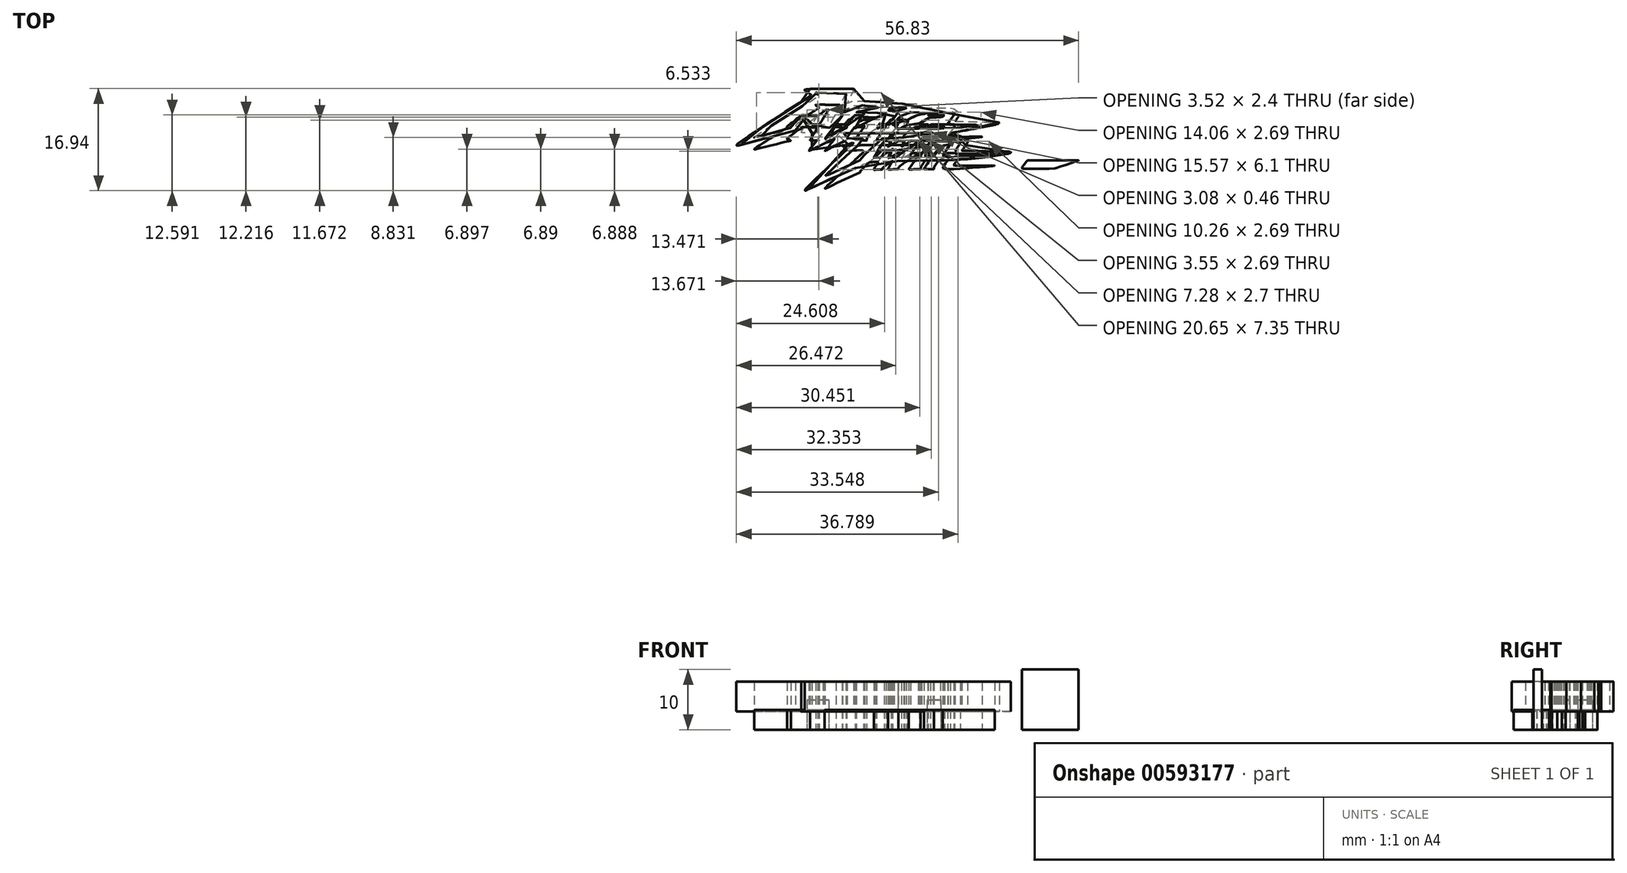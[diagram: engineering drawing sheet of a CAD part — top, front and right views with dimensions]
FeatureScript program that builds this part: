
annotation { "Feature Type Name" : "Feature", "Feature Type Description" : "" }
export const myFeature = defineFeature(function(context is Context, id is Id, definition is map)
    precondition{}
    {
        {
            var Q0;
            Q0=qCreatedBy(makeId("Top.planeOp"),FACE);
            var sketch = newSketch(context, id + "F0", { "sketchPlane" : qUnion([Q0])});
            skFitSpline(sketch, "E0", {"points": [v(-31.44, 20.71) * mm, v(-28.3, 20.77) * mm, v(-24.77, 20.79) * mm, v(-21.15, 20.83) * mm, v(-17.69, 20.85) * mm, v(-13.86, 20.87) * mm, v(-10.72, 20.85) * mm, v(-9.64, 20.77) * mm, v(-9.44, 20.67) * mm, v(-9.36, 20.45) * mm, v(-9.71, 19.84) * mm, v(-10.66, 17.85) * mm, v(-11.86, 15.37) * mm, v(-12.62, 13.83) * mm, v(-12.87, 13.46) * mm, v(-12.36, 13.66) * mm, v(-10.48, 14.38) * mm, v(-9.76, 14.62) * mm, v(-8.3, 14.67) * mm, v(-0.15, 14.62) * mm, v(8.5, 14.6) * mm, v(10.43, 14.62) * mm, v(10.86, 14.5) * mm, v(10.52, 14.24) * mm, v(9.13, 13.52) * mm, v(8.62, 13.24) * mm, v(9.3, 13.23) * mm, v(13.38, 13.2) * mm, v(17.6, 13.21) * mm, v(21.22, 13.2) * mm, v(22.36, 13.21) * mm, v(22.72, 13.17) * mm, v(22.9, 13.05) * mm, v(22.8, 12.92) * mm, v(22, 12.5) * mm, v(19.52, 11.38) * mm, v(19.17, 11.22) * mm, v(19.52, 11.18) * mm, v(21.42, 11.2) * mm, v(27.58, 11.15) * mm, v(35.7, 11.2) * mm, v(39.4, 11.2) * mm, v(39.96, 11.2) * mm, v(40.45, 11.02) * mm, v(41.07, 10.67) * mm, v(43.51, 8.93) * mm, v(43.88, 8.62) * mm, v(44.1, 8.35) * mm, v(44.07, 8.16) * mm, v(43.88, 7.78) * mm, v(43.2, 6.82) * mm, v(41.7, 4.75) * mm, v(41.4, 4.44) * mm, v(41.8, 4.44) * mm, v(46.51, 4.34) * mm, v(54.03, 4.15) * mm, v(62.87, 3.9) * mm, v(63.5, 3.86) * mm, v(63.75, 3.7) * mm, v(63.8, 3.5) * mm, v(63.56, 3.27) * mm, v(62.78, 3.02) * mm, v(61.33, 2.68) * mm, v(50.17, 0.51) * mm, v(48.29, 0.16) * mm, v(43.82, -0.7) * mm, v(41.17, -1.17) * mm, v(40.71, -1.31) * mm, v(40.3, -1.52) * mm, v(38.4, -2.7) * mm, v(38.08, -2.95) * mm, v(38.48, -2.96) * mm, v(42.95, -2.96) * mm, v(43.87, -3) * mm, v(44.42, -3.15) * mm, v(45.17, -3.73) * mm, v(47.66, -5.83) * mm, v(47.85, -6) * mm, v(47.88, -6.2) * mm, v(47.65, -6.53) * mm, v(45.18, -9.97) * mm, v(44.95, -10.32) * mm, v(45.44, -10.34) * mm, v(49.6, -10.42) * mm, v(60.85, -10.66) * mm, v(68.92, -10.88) * mm, v(69.35, -10.9) * mm, v(69.58, -11.06) * mm, v(69.63, -11.3) * mm, v(69.4, -11.5) * mm, v(68.72, -11.77) * mm, v(67.84, -11.94) * mm, v(61.37, -13.03) * mm, v(54.69, -13.9) * mm, v(46.25, -14.7) * mm, v(39.74, -15.1) * mm, v(35.06, -15.2) * mm, v(29.92, -15.28) * mm, v(24.8, -15.36) * mm, v(22.23, -15.43) * mm, v(14.78, -15.56) * mm, v(7.73, -15.76) * mm, v(1.76, -15.96) * mm, v(-0.16, -16.08) * mm, v(-1.23, -16.17) * mm, v(-1.7, -16.22) * mm, v(-2.2, -16.36) * mm, v(-3.15, -16.73) * mm, v(-5.36, -17.68) * mm, v(-8.55, -19) * mm, v(-11.16, -20.13) * mm, v(-15.96, -22.24) * mm, v(-19.22, -23.72) * mm, v(-24.73, -26.23) * mm, v(-29.57, -28.5) * mm, v(-31.83, -29.52) * mm, v(-33.6, -30.36) * mm, v(-33.79, -30.44) * mm, v(-33.93, -30.42) * mm, v(-34.06, -30.3) * mm, v(-34.08, -30.09) * mm, v(-33.96, -29.86) * mm, v(-33.08, -28.95) * mm, v(-30.44, -26.24) * mm, v(-27.52, -23.44) * mm, v(-24.82, -20.86) * mm, v(-21.12, -17.38) * mm, v(-17.92, -14.4) * mm, v(-14.38, -11.08) * mm, v(-11, -7.9) * mm, v(-9.75, -6.67) * mm, v(-9.62, -6.52) * mm, v(-9.85, -6.53) * mm, v(-10.86, -6.51) * mm, v(-10.98, -6.5) * mm, v(-11.63, -6.92) * mm, v(-11.95, -7.17) * mm, v(-12.1, -7.28) * mm, v(-12.24, -7.26) * mm, v(-12.64, -6.9) * mm, v(-15.8, -3.99) * mm, v(-16.66, -3.2) * mm, v(-16.75, -3.13) * mm, v(-16.94, -3.2) * mm, v(-19.02, -4.23) * mm, v(-21.54, -5.46) * mm, v(-26.34, -7.81) * mm, v(-30.32, -9.78) * mm, v(-31.48, -10.3) * mm, v(-31.67, -10.36) * mm, v(-31.85, -10.36) * mm, v(-31.94, -10.3) * mm, v(-32.02, -10.18) * mm, v(-31.91, -9.98) * mm, v(-31.16, -9.08) * mm, v(-27.72, -4.86) * mm, v(-25.69, -2.27) * mm, v(-25.03, -1.4) * mm, v(-24.98, -1.27) * mm, v(-25.27, -1.27) * mm, v(-30.34, -1.33) * mm, v(-34.83, -1.37) * mm, v(-35.61, -1.39) * mm, v(-35.8, -1.35) * mm, v(-35.92, -1.19) * mm, v(-35.92, -0.93) * mm, v(-35.79, -0.6) * mm, v(-35.04, 0.69) * mm, v(-33.92, 2.35) * mm, v(-32.9, 3.85) * mm, v(-31.97, 5.16) * mm, v(-31.97, 5.22) * mm, v(-32.3, 5.21) * mm, v(-34.88, 5.21) * mm, v(-34.96, 5.2) * mm, v(-35.2, 5.11) * mm, v(-36.44, 4.2) * mm, v(-38.05, 2.99) * mm, v(-38.72, 2.42) * mm, v(-38.81, 2.3) * mm, v(-38.79, 2.2) * mm, v(-38.64, 2.13) * mm, v(-38.37, 2) * mm, v(-36.75, 1.34) * mm, v(-36.2, 1.05) * mm, v(-35.96, 0.86) * mm, v(-35.85, 0.75) * mm, v(-35.93, 0.63) * mm, v(-36.35, 0.46) * mm, v(-37.36, 0.16) * mm, v(-39.12, -0.35) * mm, v(-42.53, -1.26) * mm, v(-47.35, -2.49) * mm, v(-52.88, -3.85) * mm, v(-58.58, -5.28) * mm, v(-64.61, -6.93) * mm, v(-67.43, -7.8) * mm, v(-67.74, -7.88) * mm, v(-68.03, -7.92) * mm, v(-68.31, -7.88) * mm, v(-68.5, -7.72) * mm, v(-68.5, -7.48) * mm, v(-68.17, -7.1) * mm, v(-67.4, -6.57) * mm, v(-64.48, -4.56) * mm, v(-61.76, -2.71) * mm, v(-58.36, -0.4) * mm, v(-55.05, 1.82) * mm, v(-52.23, 3.7) * mm, v(-49.26, 5.65) * mm, v(-46.62, 7.37) * mm, v(-43.48, 9.42) * mm, v(-40.62, 11.22) * mm, v(-37.84, 13) * mm, v(-34.36, 15.19) * mm, v(-31.23, 17.12) * mm, v(-30.7, 17.45) * mm, v(-30.59, 17.53) * mm, v(-30.7, 17.64) * mm, v(-31.88, 18.45) * mm, v(-33.47, 19.51) * mm, v(-34.2, 20.02) * mm, v(-34.3, 20.16) * mm, v(-34.33, 20.32) * mm, v(-34.21, 20.45) * mm, v(-33.86, 20.55) * mm, v(-33.08, 20.64) * mm, v(-32.38, 20.68) * mm, v(-31.44, 20.71) * mm]});
            skFitSpline(sketch, "E1", {"points": [v(-27.94, 18.83) * mm, v(-25.36, 18.85) * mm, v(-22.64, 18.83) * mm, v(-20.72, 18.82) * mm, v(-18.67, 18.83) * mm, v(-15.9, 18.83) * mm, v(-14.1, 18.83) * mm, v(-13.7, 18.83) * mm, v(-13.59, 18.81) * mm, v(-13.4, 18.65) * mm, v(-13.37, 18.58) * mm, v(-13.39, 18.45) * mm, v(-13.7, 17.85) * mm, v(-14.8, 15.8) * mm, v(-15.84, 13.94) * mm, v(-17.05, 11.71) * mm, v(-17.96, 9.93) * mm, v(-18.38, 9.15) * mm, v(-18.43, 9.04) * mm, v(-18.36, 8.98) * mm, v(-18.19, 8.98) * mm, v(-16.4, 8.98) * mm, v(-14.38, 9) * mm, v(-14.13, 9) * mm, v(-14, 9) * mm, v(-13.85, 9.16) * mm, v(-13.33, 9.76) * mm, v(-12.75, 10.5) * mm, v(-12.45, 10.91) * mm, v(-12.36, 11.02) * mm, v(-12.14, 11.15) * mm, v(-11.18, 11.59) * mm, v(-10.62, 11.83) * mm, v(-9.52, 12.26) * mm, v(-9.14, 12.38) * mm, v(-8.8, 12.46) * mm, v(-8.18, 12.48) * mm, v(-6.37, 12.48) * mm, v(-3.07, 12.5) * mm, v(0.47, 12.48) * mm, v(4, 12.5) * mm, v(5.57, 12.5) * mm, v(5.7, 12.47) * mm, v(5.77, 12.4) * mm, v(5.78, 12.33) * mm, v(5.63, 12.27) * mm, v(5.55, 12.22) * mm, v(4.72, 11.87) * mm, v(3.96, 11.55) * mm, v(3.4, 11.36) * mm, v(3.14, 11.28) * mm, v(2.72, 11.26) * mm, v(1.7, 11.25) * mm, v(-1.97, 11.24) * mm, v(-4.14, 11.26) * mm, v(-4.41, 11.24) * mm, v(-4.77, 11.17) * mm, v(-5.2, 10.98) * mm, v(-5.83, 10.72) * mm, v(-6.38, 10.48) * mm, v(-6.7, 10.32) * mm, v(-7.08, 10.03) * mm, v(-7.67, 9.55) * mm, v(-8.12, 9.15) * mm, v(-8.16, 9.05) * mm, v(-8.07, 8.98) * mm, v(-7.9, 9) * mm, v(-5.92, 9) * mm, v(-2.75, 8.97) * mm, v(0.26, 8.98) * mm, v(1.36, 8.99) * mm, v(1.5, 8.97) * mm, v(1.57, 8.94) * mm, v(1.6, 8.87) * mm, v(1.57, 8.8) * mm, v(1.47, 8.68) * mm, v(1.1, 8.12) * mm, v(1.03, 8.03) * mm, v(1.1, 7.95) * mm, v(1.2, 7.98) * mm, v(1.46, 8.12) * mm, v(2.51, 8.65) * mm, v(3.07, 8.87) * mm, v(3.35, 8.95) * mm, v(3.77, 8.97) * mm, v(5.54, 8.99) * mm, v(7.3, 8.97) * mm, v(9.54, 8.98) * mm, v(12.54, 8.99) * mm, v(12.68, 8.98) * mm, v(12.77, 8.95) * mm, v(12.82, 8.88) * mm, v(12.8, 8.83) * mm, v(12.7, 8.7) * mm, v(12.39, 8.3) * mm, v(11.56, 7.18) * mm, v(10.72, 6) * mm, v(9.85, 4.83) * mm, v(9.03, 3.65) * mm, v(8.33, 2.51) * mm, v(8.12, 2.16) * mm, v(7.97, 1.78) * mm, v(7.9, 1.55) * mm, v(7.9, 1.26) * mm, v(7.92, 1.1) * mm, v(7.96, 1.01) * mm, v(7.95, 0.92) * mm, v(7.88, 0.85) * mm, v(7.64, 0.85) * mm, v(7.26, 0.86) * mm, v(5.58, 0.85) * mm, v(4, 0.85) * mm, v(2.88, 0.84) * mm, v(2.23, 0.83) * mm, v(2.14, 0.87) * mm, v(2.05, 0.92) * mm, v(2, 1) * mm, v(2, 1.11) * mm, v(2.11, 1.26) * mm, v(2.32, 1.6) * mm, v(3.29, 3.02) * mm, v(4.07, 4.21) * mm, v(4.93, 5.49) * mm, v(5.7, 6.66) * mm, v(6.27, 7.5) * mm, v(6.62, 8.04) * mm, v(6.77, 8.25) * mm, v(6.84, 8.35) * mm, v(6.8, 8.39) * mm, v(6.75, 8.36) * mm, v(6.6, 8.3) * mm, v(6.12, 8.06) * mm, v(5.7, 7.86) * mm, v(5.39, 7.68) * mm, v(5.17, 7.57) * mm, v(4.7, 7.51) * mm, v(4.02, 7.45) * mm, v(3.55, 7.4) * mm, v(3.34, 7.36) * mm, v(3.18, 7.3) * mm, v(2.6, 7.04) * mm, v(1.12, 6.3) * mm, v(-0.07, 5.6) * mm, v(-0.36, 5.41) * mm, v(-0.58, 5.19) * mm, v(-0.91, 4.83) * mm, v(-1.73, 3.65) * mm, v(-2.5, 2.48) * mm, v(-2.83, 1.87) * mm, v(-2.94, 1.49) * mm, v(-2.97, 1.2) * mm, v(-2.94, 0.93) * mm, v(-2.93, 0.86) * mm, v(-3.01, 0.83) * mm, v(-3.3, 0.84) * mm, v(-4.13, 0.84) * mm, v(-6.48, 0.84) * mm, v(-8.4, 0.84) * mm, v(-8.54, 0.85) * mm, v(-8.67, 0.9) * mm, v(-8.74, 0.95) * mm, v(-8.78, 1.04) * mm, v(-8.74, 1.15) * mm, v(-8.6, 1.33) * mm, v(-8.25, 1.87) * mm, v(-7.37, 3.17) * mm, v(-6.3, 4.76) * mm, v(-5.43, 6.05) * mm, v(-4.42, 7.53) * mm, v(-4.17, 7.86) * mm, v(-3.95, 8.14) * mm, v(-3.91, 8.2) * mm, v(-3.93, 8.22) * mm, v(-3.98, 8.25) * mm, v(-4.12, 8.19) * mm, v(-4.58, 7.97) * mm, v(-4.8, 7.86) * mm, v(-5.04, 7.75) * mm, v(-5.15, 7.68) * mm, v(-5.28, 7.57) * mm, v(-5.41, 7.57) * mm, v(-6.5, 7.58) * mm, v(-7.44, 7.6) * mm, v(-8.45, 7.58) * mm, v(-8.72, 7.59) * mm, v(-8.86, 7.58) * mm, v(-9.02, 7.53) * mm, v(-9.2, 7.4) * mm, v(-9.4, 7.17) * mm, v(-10.12, 6.14) * mm, v(-10.87, 5.13) * mm, v(-12.03, 3.51) * mm, v(-12.67, 2.61) * mm, v(-12.94, 2.1) * mm, v(-13, 1.78) * mm, v(-12.98, 1.39) * mm, v(-12.98, 1.24) * mm, v(-12.98, 1.18) * mm, v(-13.05, 1.12) * mm, v(-13.57, 0.85) * mm, v(-16.05, -0.34) * mm, v(-18.68, -1.62) * mm, v(-21.07, -2.85) * mm, v(-23.2, -4.06) * mm, v(-23.86, -4.42) * mm, v(-23.99, -4.46) * mm, v(-23.97, -4.38) * mm, v(-23.9, -4.3) * mm, v(-23.55, -3.86) * mm, v(-22.4, -2.47) * mm, v(-21.58, -1.48) * mm, v(-21.03, -0.75) * mm, v(-20.06, 0.46) * mm, v(-19.46, 1.23) * mm, v(-17.66, 3.63) * mm, v(-15.85, 6.13) * mm, v(-15.14, 7.15) * mm, v(-15.08, 7.24) * mm, v(-15.1, 7.37) * mm, v(-15.22, 7.48) * mm, v(-15.39, 7.55) * mm, v(-15.54, 7.59) * mm, v(-16.37, 7.58) * mm, v(-18.12, 7.59) * mm, v(-18.98, 7.59) * mm, v(-19.06, 7.6) * mm, v(-19.12, 7.57) * mm, v(-19.19, 7.46) * mm, v(-19.71, 6.32) * mm, v(-20.6, 4.39) * mm, v(-21.2, 3) * mm, v(-21.35, 2.6) * mm, v(-21.5, 2.03) * mm, v(-21.7, 1.2) * mm, v(-21.75, 1.05) * mm, v(-21.8, 0.96) * mm, v(-21.91, 0.89) * mm, v(-22.11, 0.86) * mm, v(-22.6, 0.87) * mm, v(-25.77, 0.85) * mm, v(-28.27, 0.82) * mm, v(-30.4, 0.78) * mm, v(-31.24, 0.76) * mm, v(-31.37, 0.78) * mm, v(-31.45, 0.84) * mm, v(-31.48, 0.93) * mm, v(-31.44, 1.05) * mm, v(-31.24, 1.34) * mm, v(-30.56, 2.5) * mm, v(-30.22, 3.09) * mm, v(-29.67, 4.03) * mm, v(-29.06, 4.98) * mm, v(-28.3, 6.24) * mm, v(-27.74, 7.1) * mm, v(-27.63, 7.3) * mm, v(-27.6, 7.44) * mm, v(-27.66, 7.53) * mm, v(-27.78, 7.57) * mm, v(-28.8, 7.57) * mm, v(-32.18, 7.55) * mm, v(-34.64, 7.59) * mm, v(-35.2, 7.6) * mm, v(-35.48, 7.55) * mm, v(-35.8, 7.42) * mm, v(-36.13, 7.21) * mm, v(-36.46, 6.95) * mm, v(-37.18, 6.43) * mm, v(-39.8, 4.34) * mm, v(-41.94, 2.73) * mm, v(-42.38, 2.35) * mm, v(-42.88, 1.92) * mm, v(-43.03, 1.74) * mm, v(-43.06, 1.59) * mm, v(-42.98, 1.45) * mm, v(-42.76, 1.34) * mm, v(-41.95, 1.15) * mm, v(-41.37, 1.02) * mm, v(-41.17, 0.92) * mm, v(-41.08, 0.85) * mm, v(-41.08, 0.78) * mm, v(-41.16, 0.73) * mm, v(-41.47, 0.67) * mm, v(-41.8, 0.57) * mm, v(-44.01, 0.07) * mm, v(-45.43, -0.27) * mm, v(-48.03, -0.9) * mm, v(-51.88, -1.85) * mm, v(-54.82, -2.56) * mm, v(-58.1, -3.36) * mm, v(-59.13, -3.63) * mm, v(-59.46, -3.7) * mm, v(-59.64, -3.68) * mm, v(-59.65, -3.61) * mm, v(-59.58, -3.5) * mm, v(-59.4, -3.34) * mm, v(-58.34, -2.59) * mm, v(-56.94, -1.67) * mm, v(-54.92, -0.34) * mm, v(-53.9, 0.34) * mm, v(-51.67, 1.76) * mm, v(-49.53, 3.14) * mm, v(-48.87, 3.58) * mm, v(-48.73, 3.67) * mm, v(-47.04, 4.75) * mm, v(-44.1, 6.6) * mm, v(-41.55, 8.22) * mm, v(-38.39, 10.15) * mm, v(-35.9, 11.7) * mm, v(-33.5, 13.18) * mm, v(-30.87, 14.8) * mm, v(-27.86, 16.62) * mm, v(-26.98, 17.22) * mm, v(-26.93, 17.35) * mm, v(-26.94, 17.46) * mm, v(-27.02, 17.57) * mm, v(-27.47, 17.84) * mm, v(-27.98, 18.15) * mm, v(-28.6, 18.54) * mm, v(-28.65, 18.63) * mm, v(-28.66, 18.74) * mm, v(-28.59, 18.83) * mm, v(-28.36, 18.84) * mm, v(-27.94, 18.83) * mm]});
            skFitSpline(sketch, "E2", {"points": [v(-22.35, 15.82) * mm, v(-22.84, 15.12) * mm, v(-23.43, 14.18) * mm, v(-24.2, 13.02) * mm, v(-24.91, 11.9) * mm, v(-26, 10.2) * mm, v(-26.5, 9.37) * mm, v(-26.57, 9.25) * mm, v(-26.7, 9.13) * mm, v(-26.97, 9) * mm, v(-27.15, 8.98) * mm, v(-27.78, 8.98) * mm, v(-30.38, 8.98) * mm, v(-32.52, 8.99) * mm, v(-32.62, 8.99) * mm, v(-32.84, 9) * mm, v(-32.96, 9.05) * mm, v(-33.05, 9.11) * mm, v(-33.07, 9.23) * mm, v(-33, 9.36) * mm, v(-32.83, 9.5) * mm, v(-32.07, 10.06) * mm, v(-30.65, 11.06) * mm, v(-29.08, 12.22) * mm, v(-28.27, 12.82) * mm, v(-26.87, 13.82) * mm, v(-25.71, 14.67) * mm, v(-24.21, 15.76) * mm, v(-23.77, 16.09) * mm, v(-23.6, 16.2) * mm, v(-23.35, 16.27) * mm, v(-23.1, 16.3) * mm, v(-22.62, 16.3) * mm, v(-22.22, 16.32) * mm, v(-22.13, 16.28) * mm, v(-22.11, 16.21) * mm, v(-22.15, 16.15) * mm, v(-22.25, 16) * mm, v(-22.35, 15.82) * mm]});
            skFitSpline(sketch, "E3", {"points": [v(12, 11.25) * mm, v(14.22, 11.25) * mm, v(16.62, 11.24) * mm, v(16.78, 11.24) * mm, v(16.86, 11.21) * mm, v(16.96, 11.13) * mm, v(16.95, 11.09) * mm, v(16.84, 11.03) * mm, v(16.26, 10.83) * mm, v(14.13, 10.16) * mm, v(13.26, 9.87) * mm, v(13.01, 9.8) * mm, v(12.88, 9.79) * mm, v(12.62, 9.75) * mm, v(12, 9.74) * mm, v(9.53, 9.74) * mm, v(8.25, 9.74) * mm, v(8.1, 9.75) * mm, v(8, 9.8) * mm, v(7.93, 9.9) * mm, v(7.96, 10) * mm, v(8.08, 10.19) * mm, v(8.3, 10.52) * mm, v(8.66, 11.04) * mm, v(8.75, 11.14) * mm, v(8.92, 11.2) * mm, v(9.11, 11.22) * mm, v(9.68, 11.23) * mm, v(12, 11.25) * mm]});
            skFitSpline(sketch, "E4", {"points": [v(19.36, 8.99) * mm, v(22.68, 8.97) * mm, v(26.98, 8.98) * mm, v(27.74, 8.98) * mm, v(27.87, 8.95) * mm, v(27.9, 8.9) * mm, v(27.9, 8.85) * mm, v(27.81, 8.79) * mm, v(26.72, 8.05) * mm, v(26.31, 7.8) * mm, v(26.14, 7.7) * mm, v(25.95, 7.64) * mm, v(25.68, 7.6) * mm, v(25.22, 7.58) * mm, v(23.34, 7.58) * mm, v(22.34, 7.58) * mm, v(22.07, 7.58) * mm, v(21.9, 7.56) * mm, v(21.57, 7.43) * mm, v(20.7, 7.11) * mm, v(19.5, 6.6) * mm, v(19.23, 6.46) * mm, v(18.91, 6.25) * mm, v(18.35, 5.78) * mm, v(16.43, 4.07) * mm, v(15.81, 3.42) * mm, v(15.68, 3.27) * mm, v(15.64, 3.16) * mm, v(15.67, 3) * mm, v(15.77, 2.85) * mm, v(16.02, 2.67) * mm, v(16.3, 2.56) * mm, v(16.65, 2.52) * mm, v(17.73, 2.53) * mm, v(21.55, 2.52) * mm, v(22.6, 2.53) * mm, v(22.94, 2.53) * mm, v(23, 2.53) * mm, v(23.05, 2.6) * mm, v(23.41, 3.02) * mm, v(23.63, 3.26) * mm, v(24.59, 4.23) * mm, v(25.3, 4.9) * mm, v(25.69, 5.2) * mm, v(25.97, 5.35) * mm, v(26.75, 5.64) * mm, v(27.39, 5.85) * mm, v(28.23, 6.08) * mm, v(28.93, 6.15) * mm, v(29.7, 6.23) * mm, v(31.7, 6.4) * mm, v(33.63, 6.54) * mm, v(34.2, 6.6) * mm, v(34.7, 6.66) * mm, v(35.26, 6.83) * mm, v(35.67, 7.05) * mm, v(36.07, 7.23) * mm, v(36.27, 7.4) * mm, v(36.3, 7.48) * mm, v(36.3, 7.54) * mm, v(36.25, 7.57) * mm, v(36.1, 7.57) * mm, v(34.31, 7.56) * mm, v(32.6, 7.56) * mm, v(30.43, 7.56) * mm, v(28.46, 7.56) * mm, v(28.03, 7.55) * mm, v(27.98, 7.56) * mm, v(27.91, 7.6) * mm, v(27.86, 7.67) * mm, v(27.85, 7.73) * mm, v(27.9, 7.8) * mm, v(28.04, 7.9) * mm, v(28.89, 8.5) * mm, v(29.46, 8.87) * mm, v(29.62, 8.94) * mm, v(29.72, 8.98) * mm, v(29.84, 8.99) * mm, v(30.41, 9) * mm, v(32.93, 9) * mm, v(35.39, 8.99) * mm, v(38.86, 8.99) * mm, v(39.63, 8.98) * mm, v(39.87, 8.97) * mm, v(40.04, 8.93) * mm, v(40.22, 8.87) * mm, v(40.42, 8.75) * mm, v(41.05, 8.3) * mm, v(41.22, 8.16) * mm, v(41.28, 8.07) * mm, v(41.3, 7.97) * mm, v(41.27, 7.87) * mm, v(41.14, 7.68) * mm, v(41.01, 7.5) * mm, v(40.1, 6.26) * mm, v(39.1, 4.97) * mm, v(38.1, 3.7) * mm, v(37.82, 3.3) * mm, v(37.74, 3.21) * mm, v(37.71, 3.11) * mm, v(37.74, 3.03) * mm, v(37.83, 2.93) * mm, v(38.07, 2.8) * mm, v(38.36, 2.63) * mm, v(38.56, 2.56) * mm, v(38.7, 2.54) * mm, v(39.3, 2.56) * mm, v(41.81, 2.58) * mm, v(44.71, 2.63) * mm, v(47.11, 2.67) * mm, v(49.35, 2.7) * mm, v(51.41, 2.72) * mm, v(52.93, 2.75) * mm, v(54.17, 2.77) * mm, v(54.89, 2.79) * mm, v(54.96, 2.8) * mm, v(55.02, 2.78) * mm, v(55.05, 2.74) * mm, v(55.03, 2.71) * mm, v(54.96, 2.68) * mm, v(54.82, 2.66) * mm, v(53.2, 2.43) * mm, v(51.02, 2.17) * mm, v(48.66, 1.9) * mm, v(45.26, 1.54) * mm, v(41.9, 1.17) * mm, v(39.22, 0.86) * mm, v(38.78, 0.84) * mm, v(36.51, 0.83) * mm, v(35.17, 0.83) * mm, v(34.5, 0.86) * mm, v(34.22, 0.9) * mm, v(34.05, 0.96) * mm, v(33.78, 1.18) * mm, v(33.61, 1.38) * mm, v(33.52, 1.52) * mm, v(33.42, 1.69) * mm, v(33.38, 1.76) * mm, v(33.36, 1.75) * mm, v(33.27, 1.66) * mm, v(32.95, 1.44) * mm, v(32.42, 1.15) * mm, v(32.03, 0.98) * mm, v(31.5, 0.89) * mm, v(30.58, 0.84) * mm, v(28.38, 0.84) * mm, v(25.63, 0.85) * mm, v(23.37, 0.85) * mm, v(19.81, 0.85) * mm, v(16.57, 0.85) * mm, v(13.2, 0.84) * mm, v(12.09, 0.83) * mm, v(11.79, 0.85) * mm, v(11.35, 1) * mm, v(10.86, 1.32) * mm, v(10.16, 2.03) * mm, v(9.82, 2.45) * mm, v(9.75, 2.63) * mm, v(9.75, 2.76) * mm, v(9.81, 2.9) * mm, v(9.97, 3.08) * mm, v(10.5, 3.63) * mm, v(11.11, 4.23) * mm, v(11.88, 4.94) * mm, v(13, 5.95) * mm, v(14.06, 6.9) * mm, v(14.34, 7.11) * mm, v(14.56, 7.3) * mm, v(15.03, 7.59) * mm, v(15.46, 7.77) * mm, v(16.45, 8.18) * mm, v(17.81, 8.69) * mm, v(18.25, 8.85) * mm, v(18.6, 8.95) * mm, v(18.93, 8.99) * mm, v(19.36, 8.99) * mm]});
            skFitSpline(sketch, "E5", {"points": [v(30.67, 4.75) * mm, v(32.06, 4.83) * mm, v(33.57, 4.98) * mm, v(34.1, 5) * mm, v(34.25, 4.98) * mm, v(34.3, 4.94) * mm, v(34.3, 4.86) * mm, v(34.18, 4.73) * mm, v(33.6, 4.16) * mm, v(32.93, 3.51) * mm, v(32.56, 3.19) * mm, v(32.18, 2.95) * mm, v(31.7, 2.76) * mm, v(31.22, 2.65) * mm, v(30.5, 2.56) * mm, v(28.92, 2.54) * mm, v(27.99, 2.53) * mm, v(27.72, 2.58) * mm, v(27.49, 2.74) * mm, v(27.38, 2.83) * mm, v(27.35, 2.9) * mm, v(27.4, 3.02) * mm, v(27.57, 3.28) * mm, v(27.68, 3.42) * mm, v(27.96, 3.64) * mm, v(28.47, 3.97) * mm, v(29.04, 4.3) * mm, v(29.6, 4.54) * mm, v(30.1, 4.68) * mm, v(30.67, 4.75) * mm]});
            skFitSpline(sketch, "E6", {"points": [v(-14.6, -1.57) * mm, v(-11.2, -1.57) * mm, v(-8.48, -1.56) * mm, v(-4.15, -1.55) * mm, v(-0.76, -1.54) * mm, v(2.28, -1.52) * mm, v(4.75, -1.5) * mm, v(6.58, -1.5) * mm, v(8.88, -1.5) * mm, v(11.94, -1.5) * mm, v(14.7, -1.47) * mm, v(17.8, -1.44) * mm, v(22.1, -1.44) * mm, v(25.9, -1.42) * mm, v(29.15, -1.42) * mm, v(29.99, -1.41) * mm, v(30.42, -1.4) * mm, v(30.5, -1.42) * mm, v(30.5, -1.45) * mm, v(30.4, -1.48) * mm, v(28.76, -1.77) * mm, v(25.05, -2.3) * mm, v(21.95, -2.78) * mm, v(17.9, -3.34) * mm, v(13.88, -3.92) * mm, v(12.93, -4.08) * mm, v(12.07, -4.13) * mm, v(10.14, -4.11) * mm, v(8.64, -4.14) * mm, v(5.74, -4.19) * mm, v(5.16, -4.21) * mm, v(4.9, -4.26) * mm, v(4.63, -4.38) * mm, v(4.25, -4.64) * mm, v(3.5, -5.28) * mm, v(2.2, -6.52) * mm, v(0.46, -8.22) * mm, v(-1.37, -9.96) * mm, v(-3.6, -12.02) * mm, v(-5.55, -13.84) * mm, v(-5.8, -14.14) * mm, v(-6.04, -14.49) * mm, v(-6.16, -14.84) * mm, v(-6.29, -15.13) * mm, v(-6.33, -15.2) * mm, v(-6.42, -15.26) * mm, v(-6.73, -15.42) * mm, v(-10.19, -16.97) * mm, v(-13.51, -18.47) * mm, v(-17.5, -20.35) * mm, v(-21.58, -22.33) * mm, v(-23.28, -23.15) * mm, v(-23.75, -23.37) * mm, v(-23.85, -23.4) * mm, v(-24, -23.4) * mm, v(-24.06, -23.38) * mm, v(-24.08, -23.3) * mm, v(-24.05, -23.2) * mm, v(-23.92, -23.03) * mm, v(-23.24, -22.4) * mm, v(-21.57, -20.8) * mm, v(-20.09, -19.4) * mm, v(-17.6, -17.07) * mm, v(-15.2, -14.85) * mm, v(-13.02, -12.8) * mm, v(-10.94, -10.93) * mm, v(-8.92, -9.02) * mm, v(-6.32, -6.58) * mm, v(-4.75, -5.1) * mm, v(-4.58, -4.88) * mm, v(-4.54, -4.78) * mm, v(-4.56, -4.66) * mm, v(-4.85, -4.45) * mm, v(-5.14, -4.28) * mm, v(-5.25, -4.23) * mm, v(-5.49, -4.24) * mm, v(-7, -4.24) * mm, v(-10.43, -4.22) * mm, v(-11.54, -4.22) * mm, v(-11.66, -4.23) * mm, v(-11.73, -4.25) * mm, v(-11.84, -4.36) * mm, v(-11.98, -4.47) * mm, v(-12.05, -4.5) * mm, v(-12.1, -4.49) * mm, v(-12.23, -4.4) * mm, v(-12.56, -4.1) * mm, v(-14.16, -2.73) * mm, v(-15.13, -1.84) * mm, v(-15.2, -1.76) * mm, v(-15.23, -1.66) * mm, v(-15.19, -1.6) * mm, v(-15.1, -1.56) * mm, v(-14.6, -1.57) * mm]});
            skFitSpline(sketch, "E7", {"points": [v(6.07, -5.46) * mm, v(8.68, -5.48) * mm, v(9.15, -5.5) * mm, v(9.27, -5.5) * mm, v(9.33, -5.53) * mm, v(9.36, -5.6) * mm, v(9.32, -5.69) * mm, v(9.2, -5.9) * mm, v(8.52, -6.99) * mm, v(8.03, -7.79) * mm, v(7.8, -8.15) * mm, v(7.77, -8.25) * mm, v(7.78, -8.35) * mm, v(7.86, -8.41) * mm, v(8, -8.35) * mm, v(8.57, -7.98) * mm, v(9.33, -7.52) * mm, v(10.97, -6.48) * mm, v(11.65, -6.02) * mm, v(12.27, -5.64) * mm, v(12.43, -5.55) * mm, v(12.66, -5.5) * mm, v(13.2, -5.47) * mm, v(14, -5.48) * mm, v(15.85, -5.48) * mm, v(16.05, -5.52) * mm, v(16.1, -5.56) * mm, v(16.14, -5.64) * mm, v(16.06, -5.78) * mm, v(15.87, -6.06) * mm, v(15.23, -7.14) * mm, v(14.78, -7.84) * mm, v(14.57, -8.2) * mm, v(14.51, -8.3) * mm, v(14.52, -8.4) * mm, v(14.6, -8.43) * mm, v(14.8, -8.31) * mm, v(15.52, -7.85) * mm, v(16.5, -7.26) * mm, v(17.29, -6.78) * mm, v(18.2, -6.26) * mm, v(19, -5.76) * mm, v(19.28, -5.58) * mm, v(19.41, -5.51) * mm, v(19.6, -5.48) * mm, v(19.84, -5.48) * mm, v(23.1, -5.47) * mm, v(23.46, -5.48) * mm, v(23.52, -5.48) * mm, v(23.56, -5.53) * mm, v(23.5, -5.58) * mm, v(23.22, -5.77) * mm, v(22.43, -6.3) * mm, v(20.83, -7.31) * mm, v(19.24, -8.32) * mm, v(17.72, -9.29) * mm, v(15.52, -10.77) * mm, v(14.27, -11.65) * mm, v(13.88, -11.95) * mm, v(13.56, -12.26) * mm, v(13.28, -12.57) * mm, v(13.1, -12.83) * mm, v(12.97, -13.1) * mm, v(12.94, -13.32) * mm, v(12.93, -13.51) * mm, v(12.93, -13.56) * mm, v(12.88, -13.58) * mm, v(12.76, -13.6) * mm, v(11.73, -13.6) * mm, v(10.8, -13.63) * mm, v(9.54, -13.7) * mm, v(8.3, -13.72) * mm, v(7.96, -13.73) * mm, v(7.82, -13.7) * mm, v(7.72, -13.65) * mm, v(7.7, -13.58) * mm, v(7.71, -13.46) * mm, v(7.93, -13.07) * mm, v(8.34, -12.42) * mm, v(8.9, -11.42) * mm, v(9.36, -10.66) * mm, v(9.67, -10.16) * mm, v(9.96, -9.7) * mm, v(10.14, -9.4) * mm, v(10.18, -9.35) * mm, v(10.18, -9.32) * mm, v(10.15, -9.34) * mm, v(10.01, -9.41) * mm, v(9.36, -9.84) * mm, v(8.5, -10.42) * mm, v(7.48, -11.11) * mm, v(7, -11.48) * mm, v(6.18, -12.06) * mm, v(5.68, -12.42) * mm, v(5.4, -12.66) * mm, v(5.26, -12.88) * mm, v(5.14, -13.05) * mm, v(5.02, -13.34) * mm, v(4.95, -13.55) * mm, v(4.92, -13.66) * mm, v(4.86, -13.69) * mm, v(4.66, -13.7) * mm, v(3.26, -13.77) * mm, v(2.09, -13.86) * mm, v(1, -13.93) * mm, v(0.85, -13.91) * mm, v(0.75, -13.88) * mm, v(0.68, -13.81) * mm, v(0.66, -13.71) * mm, v(0.72, -13.57) * mm, v(0.86, -13.3) * mm, v(1.6, -12.07) * mm, v(2.29, -10.93) * mm, v(2.84, -10) * mm, v(3.3, -9.2) * mm, v(4.04, -7.98) * mm, v(4.69, -6.95) * mm, v(5.22, -6.06) * mm, v(5.58, -5.5) * mm, v(5.66, -5.47) * mm, v(5.84, -5.45) * mm, v(6.07, -5.46) * mm]});
            skFitSpline(sketch, "E8", {"points": [v(27.89, -3.02) * mm, v(30.66, -3.01) * mm, v(33.29, -3.01) * mm, v(34.05, -2.99) * mm, v(34.21, -3) * mm, v(34.21, -3.03) * mm, v(33.93, -3.12) * mm, v(32.8, -3.53) * mm, v(31.45, -3.98) * mm, v(30.54, -4.3) * mm, v(30.41, -4.35) * mm, v(30.27, -4.37) * mm, v(28.54, -4.4) * mm, v(26.16, -4.4) * mm, v(24.9, -4.4) * mm, v(24.83, -4.36) * mm, v(24.78, -4.29) * mm, v(24.81, -4.16) * mm, v(25.28, -3.56) * mm, v(25.66, -3.08) * mm, v(25.73, -3.02) * mm, v(25.8, -3) * mm, v(27.89, -3.02) * mm]});
            skFitSpline(sketch, "E9", {"points": [v(24.8, -5.5) * mm, v(28.52, -5.5) * mm, v(28.86, -5.5) * mm, v(29.01, -5.5) * mm, v(29.1, -5.54) * mm, v(29.14, -5.61) * mm, v(29.1, -5.7) * mm, v(28.82, -6.05) * mm, v(27.83, -7.4) * mm, v(26.59, -9.11) * mm, v(25.28, -10.96) * mm, v(24.71, -11.84) * mm, v(24.47, -12.25) * mm, v(24.3, -12.64) * mm, v(24.2, -12.98) * mm, v(24.23, -13.42) * mm, v(24.23, -13.54) * mm, v(24.23, -13.59) * mm, v(24.13, -13.6) * mm, v(22.42, -13.65) * mm, v(19.82, -13.68) * mm, v(18.58, -13.69) * mm, v(18.4, -13.66) * mm, v(18.33, -13.6) * mm, v(18.27, -13.5) * mm, v(18.3, -13.4) * mm, v(18.44, -13.2) * mm, v(19.41, -11.83) * mm, v(19.98, -11) * mm, v(21.08, -9.54) * mm, v(22.16, -8.03) * mm, v(23.26, -6.62) * mm, v(23.92, -5.86) * mm, v(24.17, -5.57) * mm, v(24.22, -5.5) * mm, v(24.3, -5.5) * mm, v(24.8, -5.5) * mm]});
            skFitSpline(sketch, "E10", {"points": [v(31.53, -5.5) * mm, v(33.25, -5.51) * mm, v(34.88, -5.5) * mm, v(35.52, -5.5) * mm, v(35.65, -5.5) * mm, v(35.77, -5.56) * mm, v(35.77, -5.62) * mm, v(35.68, -5.77) * mm, v(35.5, -6) * mm, v(35.4, -6.14) * mm, v(35.4, -6.2) * mm, v(35.44, -6.28) * mm, v(35.57, -6.25) * mm, v(35.9, -6.15) * mm, v(37.28, -5.67) * mm, v(37.62, -5.57) * mm, v(37.93, -5.51) * mm, v(38.46, -5.5) * mm, v(41.56, -5.5) * mm, v(42.63, -5.5) * mm, v(42.8, -5.51) * mm, v(43, -5.57) * mm, v(43.4, -5.86) * mm, v(44.09, -6.33) * mm, v(44.18, -6.43) * mm, v(44.22, -6.53) * mm, v(44.16, -6.65) * mm, v(43.75, -7.23) * mm, v(43.12, -8.14) * mm, v(42.08, -9.63) * mm, v(41.22, -10.8) * mm, v(40.87, -11.26) * mm, v(40.81, -11.36) * mm, v(40.83, -11.47) * mm, v(40.95, -11.6) * mm, v(41.2, -11.76) * mm, v(41.45, -11.87) * mm, v(41.79, -11.91) * mm, v(43.11, -11.9) * mm, v(46.35, -11.87) * mm, v(49.15, -11.83) * mm, v(51.56, -11.8) * mm, v(54.45, -11.79) * mm, v(56.8, -11.76) * mm, v(59.52, -11.7) * mm, v(61.18, -11.72) * mm, v(61.37, -11.73) * mm, v(61.44, -11.76) * mm, v(61.48, -11.8) * mm, v(61.46, -11.86) * mm, v(61.37, -11.91) * mm, v(61.07, -11.97) * mm, v(58.26, -12.25) * mm, v(55.58, -12.47) * mm, v(52.1, -12.74) * mm, v(48.76, -12.99) * mm, v(45.73, -13.22) * mm, v(42.7, -13.44) * mm, v(40.52, -13.6) * mm, v(39.03, -13.61) * mm, v(36.88, -13.6) * mm, v(36.7, -13.58) * mm, v(36.32, -13.48) * mm, v(35.7, -13.2) * mm, v(35.38, -13.01) * mm, v(35.32, -12.9) * mm, v(35.3, -12.8) * mm, v(35.38, -12.64) * mm, v(35.61, -12.3) * mm, v(36.07, -11.65) * mm, v(36.68, -10.79) * mm, v(37.42, -9.7) * mm, v(37.97, -8.93) * mm, v(38.58, -8.04) * mm, v(38.93, -7.57) * mm, v(39.04, -7.41) * mm, v(39.08, -7.28) * mm, v(39, -7.14) * mm, v(38.75, -7.06) * mm, v(38.34, -7.04) * mm, v(38, -7.02) * mm, v(37.72, -7.07) * mm, v(37.3, -7.26) * mm, v(36.37, -7.7) * mm, v(34.66, -8.42) * mm, v(33.8, -8.83) * mm, v(33.48, -9.02) * mm, v(33.25, -9.23) * mm, v(32.9, -9.63) * mm, v(32.06, -10.82) * mm, v(31.37, -11.84) * mm, v(31.1, -12.26) * mm, v(31, -12.56) * mm, v(30.96, -12.87) * mm, v(30.95, -13.3) * mm, v(30.94, -13.5) * mm, v(30.89, -13.57) * mm, v(30.79, -13.64) * mm, v(30.65, -13.66) * mm, v(29.9, -13.65) * mm, v(27.24, -13.66) * mm, v(26.11, -13.66) * mm, v(25.98, -13.64) * mm, v(25.88, -13.57) * mm, v(25.85, -13.47) * mm, v(25.9, -13.33) * mm, v(26.06, -13.08) * mm, v(26.73, -12.1) * mm, v(27.2, -11.4) * mm, v(28.14, -9.97) * mm, v(29.05, -8.62) * mm, v(30.39, -6.6) * mm, v(30.98, -5.7) * mm, v(31.1, -5.57) * mm, v(31.26, -5.53) * mm, v(31.53, -5.5) * mm]});
            skSolve(sketch);
        }
        {
            var Q0;
            Q0=qSketchRegion(id+"F0",true);
            var Q1;
            Q1=makeQuery(id+"F0.imprint","IMPRINT",FACE,{"disambiguationData":[TD([[makeQuery(id+"F0.imprint","IMPRINT",EDGE,{"derivedFrom":sQuery(id+"F0.wireOp",EDGE,"E5")}),-1.0]])]});
            var Q2;
            Q2=makeQuery(id+"F0.imprint","IMPRINT",FACE,{"disambiguationData":[TD([[makeQuery(id+"F0.imprint","IMPRINT",EDGE,{"derivedFrom":sQuery(id+"F0.wireOp",EDGE,"E2")}),-1.0]])]});
            extrude(context, id + "F1", {"entities" : qUnion([Q0, Q1, Q2]), "depth" : 15 * mm, "offsetDistance" : 25 * mm});
        }
        {
            var Q0;
            Q0=makeQuery(id+"F0.imprint","IMPRINT",FACE,{"disambiguationData":[TD([[makeQuery(id+"F0.imprint","IMPRINT",EDGE,{"derivedFrom":sQuery(id+"F0.wireOp",EDGE,"E1")}),-1.0]])]});
            var Q1;
            Q1=makeQuery(id+"F0.imprint","IMPRINT",FACE,{"disambiguationData":[TD([[makeQuery(id+"F0.imprint","IMPRINT",EDGE,{"derivedFrom":sQuery(id+"F0.wireOp",EDGE,"E3")}),-1.0]])]});
            var Q2;
            Q2=makeQuery(id+"F0.imprint","IMPRINT",FACE,{"disambiguationData":[TD([[makeQuery(id+"F0.imprint","IMPRINT",EDGE,{"derivedFrom":sQuery(id+"F0.wireOp",EDGE,"E4")}),-1.0]])]});
            var Q3;
            Q3=makeQuery(id+"F0.imprint","IMPRINT",FACE,{"disambiguationData":[TD([[makeQuery(id+"F0.imprint","IMPRINT",EDGE,{"derivedFrom":sQuery(id+"F0.wireOp",EDGE,"E10")}),-1.0]])]});
            var Q4;
            Q4=makeQuery(id+"F0.imprint","IMPRINT",FACE,{"disambiguationData":[TD([[makeQuery(id+"F0.imprint","IMPRINT",EDGE,{"derivedFrom":sQuery(id+"F0.wireOp",EDGE,"E9")}),-1.0]])]});
            var Q5;
            Q5=makeQuery(id+"F0.imprint","IMPRINT",FACE,{"disambiguationData":[TD([[makeQuery(id+"F0.imprint","IMPRINT",EDGE,{"derivedFrom":sQuery(id+"F0.wireOp",EDGE,"E7")}),-1.0]])]});
            var Q6;
            Q6=makeQuery(id+"F0.imprint","IMPRINT",FACE,{"disambiguationData":[TD([[makeQuery(id+"F0.imprint","IMPRINT",EDGE,{"derivedFrom":sQuery(id+"F0.wireOp",EDGE,"E6")}),-1.0]])]});
            var Q7;
            Q7=makeQuery(id+"F0.imprint","IMPRINT",FACE,{"disambiguationData":[TD([[makeQuery(id+"F0.imprint","IMPRINT",EDGE,{"derivedFrom":sQuery(id+"F0.wireOp",EDGE,"E8")}),-1.0]])]});
            extrude(context, id + "F2", {"entities" : qUnion([Q0, Q1, Q2, Q3, Q4, Q5, Q6, Q7]), "depth" : 10 * mm, "offsetDistance" : 25 * mm});
        }
        {
            var Q0;
            Q0=makeQuery(id+"F1.opExtrude","SWEPT_BODY",BODY,{"disambiguationData":[OSD([sQuery(id+"F0.wireOp",EDGE,"E0"),sQuery(id+"F0.wireOp",EDGE,"E1"),sQuery(id+"F0.wireOp",EDGE,"E3"),sQuery(id+"F0.wireOp",EDGE,"E4"),sQuery(id+"F0.wireOp",EDGE,"E6"),sQuery(id+"F0.wireOp",EDGE,"E7"),sQuery(id+"F0.wireOp",EDGE,"E8"),sQuery(id+"F0.wireOp",EDGE,"E9"),sQuery(id+"F0.wireOp",EDGE,"E10")])]});
            var Q1;
            Q1=makeQuery(id+"F1.opExtrude","SWEPT_BODY",BODY,{"disambiguationData":[OSD([sQuery(id+"F0.wireOp",EDGE,"E2")])]});
            var Q2;
            Q2=makeQuery(id+"F1.opExtrude","SWEPT_BODY",BODY,{"disambiguationData":[OSD([sQuery(id+"F0.wireOp",EDGE,"E5")])]});
            var Q3;
            Q3=makeQuery(id+"F2.opExtrude","SWEPT_BODY",BODY,{"disambiguationData":[OSD([sQuery(id+"F0.wireOp",EDGE,"E1"),sQuery(id+"F0.wireOp",EDGE,"E2")])]});
            var Q4;
            Q4=makeQuery(id+"F2.opExtrude","SWEPT_BODY",BODY,{"disambiguationData":[OSD([sQuery(id+"F0.wireOp",EDGE,"E6")])]});
            var Q5;
            Q5=makeQuery(id+"F2.opExtrude","SWEPT_BODY",BODY,{"disambiguationData":[OSD([sQuery(id+"F0.wireOp",EDGE,"E7")])]});
            var Q6;
            Q6=makeQuery(id+"F2.opExtrude","SWEPT_BODY",BODY,{"disambiguationData":[OSD([sQuery(id+"F0.wireOp",EDGE,"E9")])]});
            var Q7;
            Q7=makeQuery(id+"F2.opExtrude","SWEPT_BODY",BODY,{"disambiguationData":[OSD([sQuery(id+"F0.wireOp",EDGE,"E10")])]});
            var Q8;
            Q8=makeQuery(id+"F2.opExtrude","SWEPT_BODY",BODY,{"disambiguationData":[OSD([sQuery(id+"F0.wireOp",EDGE,"E4"),sQuery(id+"F0.wireOp",EDGE,"E5")])]});
            var Q9;
            Q9=makeQuery(id+"F2.opExtrude","SWEPT_BODY",BODY,{"disambiguationData":[OSD([sQuery(id+"F0.wireOp",EDGE,"E3")])]});
            var Q10;
            Q10=qCreatedBy(makeId("Origin.pointOp"),VERTEX);
            var Q11;
            Q11=qCreatedBy(makeId("Origin.pointOp"),VERTEX);
            transform(context, id + "F3", {"entities" : qUnion([Q0, Q1, Q2, Q3, Q4, Q5, Q6, Q7, Q8, Q9]), "transformType" : TransformType.SCALE_UNIFORMLY, "scale" : 0.33, "scalePoint" : qUnion([Q11]), "makeCopy" : false});
        }
        {
            var Q0;
            Q0=makeQuery(id+"F1.opExtrude","SWEPT_BODY",BODY,{"disambiguationData":[OSD([sQuery(id+"F0.wireOp",EDGE,"E0"),sQuery(id+"F0.wireOp",EDGE,"E1"),sQuery(id+"F0.wireOp",EDGE,"E3"),sQuery(id+"F0.wireOp",EDGE,"E4"),sQuery(id+"F0.wireOp",EDGE,"E6"),sQuery(id+"F0.wireOp",EDGE,"E7"),sQuery(id+"F0.wireOp",EDGE,"E8"),sQuery(id+"F0.wireOp",EDGE,"E9"),sQuery(id+"F0.wireOp",EDGE,"E10")])]});
            var Q1;
            Q1=qCreatedBy(makeId("Top.planeOp"),FACE);
            transform(context, id + "F4", {"entities" : qUnion([Q0]), "transformType" : TransformType.TRANSLATION_DISTANCE, "transformDirection" : qUnion([Q1]), "distance" : 3 * mm, "makeCopy" : false});
        }
        {
            var Q0;
            Q0=makeQuery(id+"F1.opExtrude","SWEPT_BODY",BODY,{"disambiguationData":[OSD([sQuery(id+"F0.wireOp",EDGE,"E0"),sQuery(id+"F0.wireOp",EDGE,"E1"),sQuery(id+"F0.wireOp",EDGE,"E3"),sQuery(id+"F0.wireOp",EDGE,"E4"),sQuery(id+"F0.wireOp",EDGE,"E6"),sQuery(id+"F0.wireOp",EDGE,"E7"),sQuery(id+"F0.wireOp",EDGE,"E8"),sQuery(id+"F0.wireOp",EDGE,"E9"),sQuery(id+"F0.wireOp",EDGE,"E10")])]});
            var Q1;
            Q1=qCreatedBy(makeId("Front.planeOp"),FACE);
            transform(context, id + "F5", {"entities" : qUnion([Q0]), "transformType" : TransformType.TRANSLATION_DISTANCE, "transformDirection" : qUnion([Q1]), "distance" : 2 * mm, "oppositeDirection" : true, "makeCopy" : false});
        }
    });
